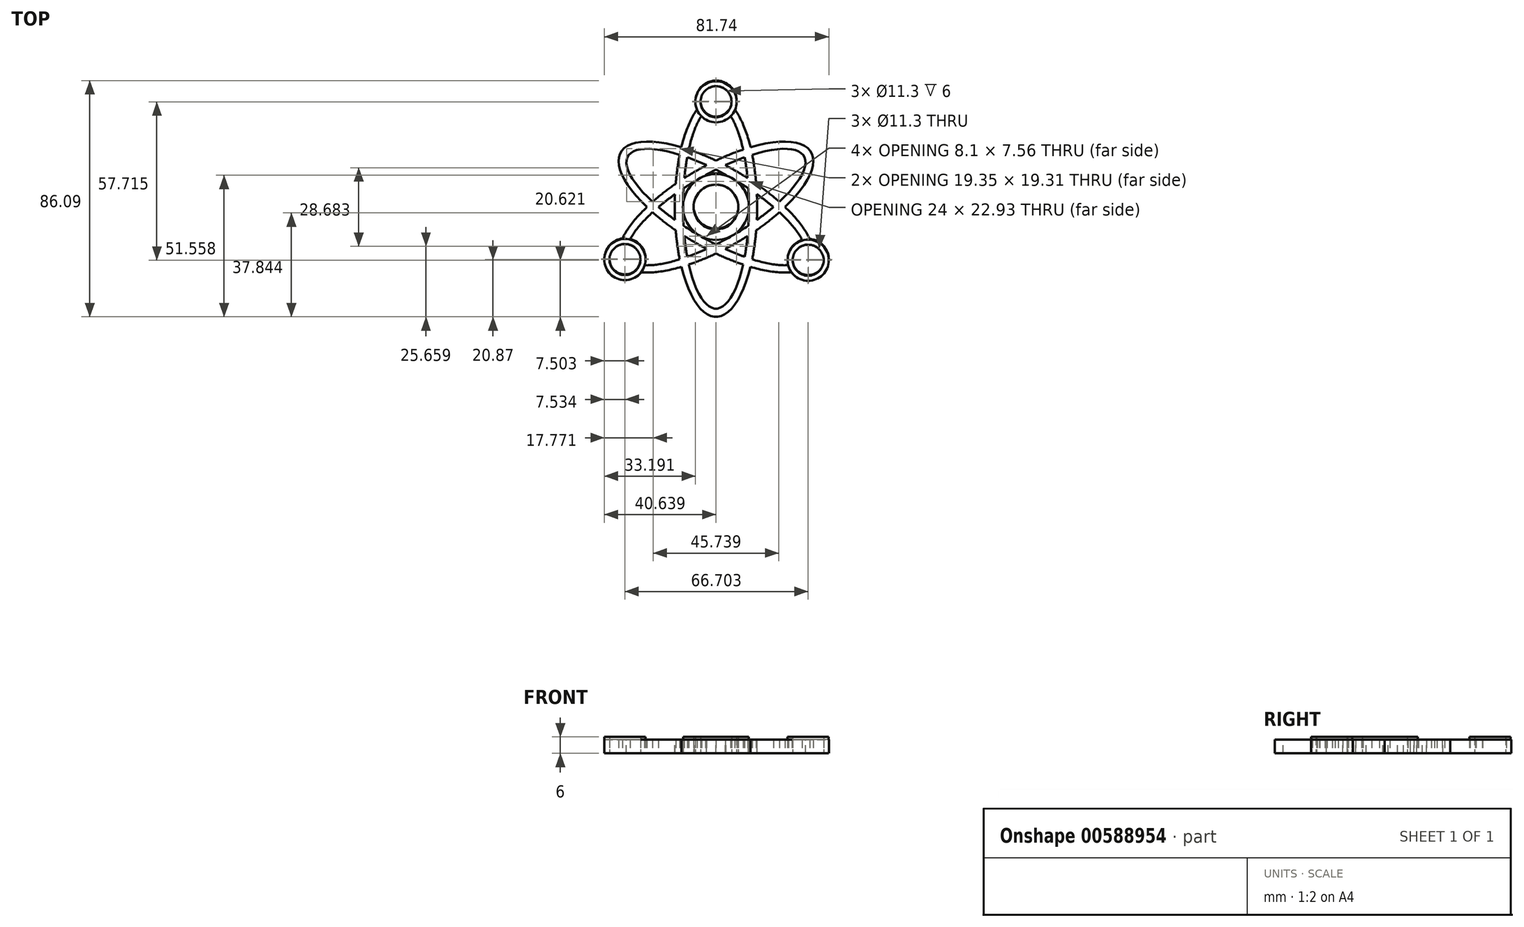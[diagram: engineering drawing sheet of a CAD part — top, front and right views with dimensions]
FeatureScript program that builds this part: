
annotation { "Feature Type Name" : "Feature", "Feature Type Description" : "" }
export const myFeature = defineFeature(function(context is Context, id is Id, definition is map)
    precondition{}
    {
        {
            var Q0;
            Q0=qCreatedBy(makeId("Top.planeOp"),FACE);
            var sketch = newSketch(context, id + "F0", { "sketchPlane" : qUnion([Q0])});
            skEllipticalArc(sketch, "E0", {});
            skEllipticalArc(sketch, "E1", {});
            skEllipticalArc(sketch, "E2", {});
            skEllipticalArc(sketch, "E3", {});
            skEllipticalArc(sketch, "E4", {});
            skEllipticalArc(sketch, "E5", {});
            skEllipticalArc(sketch, "E6.trimOffspring", {});
            skEllipticalArc(sketch, "E7.trimOffspring", {});
            skEllipticalArc(sketch, "E8.trimOffspring", {});
            skEllipticalArc(sketch, "E9.trimOffspring", {});
            skEllipticalArc(sketch, "E10.trimOffspring", {});
            skEllipticalArc(sketch, "E11.trimOffspring", {});
            skEllipticalArc(sketch, "E12.trimOffspring", {});
            skEllipticalArc(sketch, "E13.trimOffspring", {});
            skEllipticalArc(sketch, "E14.trimOffspring", {});
            skEllipticalArc(sketch, "E15.trimOffspring", {});
            skEllipticalArc(sketch, "E16.trimOffspring", {});
            skEllipticalArc(sketch, "E17.trimOffspring", {});
            skEllipticalArc(sketch, "E18.trimOffspring", {});
            skEllipticalArc(sketch, "E19.trimOffspring", {});
            skEllipticalArc(sketch, "E20.trimOffspring", {});
            skEllipticalArc(sketch, "E21.trimOffspring", {});
            skEllipticalArc(sketch, "E22.trimOffspring", {});
            skEllipticalArc(sketch, "E23.trimOffspring", {});
            skEllipticalArc(sketch, "E24.trimOffspring", {});
            skEllipticalArc(sketch, "E25.trimOffspring", {});
            skEllipticalArc(sketch, "E26.trimOffspring", {});
            skEllipticalArc(sketch, "E27.trimOffspring", {});
            skEllipticalArc(sketch, "E28.trimOffspring", {});
            skEllipticalArc(sketch, "E29.trimOffspring", {});
            skEllipticalArc(sketch, "E30.trimOffspring", {});
            skEllipticalArc(sketch, "E31.trimOffspring", {});
            skEllipticalArc(sketch, "E32.trimOffspring", {});
            skEllipticalArc(sketch, "E33.trimOffspring", {});
            skEllipticalArc(sketch, "E34.trimOffspring", {});
            skEllipticalArc(sketch, "E35.trimOffspring", {});
            skEllipticalArc(sketch, "E36.trimOffspring", {});
            skEllipticalArc(sketch, "E37.trimOffspring", {});
            skEllipticalArc(sketch, "E38.trimOffspring", {});
            skEllipticalArc(sketch, "E39.trimOffspring", {});
            skEllipticalArc(sketch, "E40.trimOffspring", {});
            skEllipticalArc(sketch, "E41.trimOffspring", {});
            skEllipticalArc(sketch, "E42.trimOffspring", {});
            skEllipticalArc(sketch, "E43.trimOffspring", {});
            skEllipticalArc(sketch, "E44.trimOffspring", {});
            skEllipticalArc(sketch, "E45.trimOffspring", {});
            skEllipticalArc(sketch, "E46.trimOffspring", {});
            skEllipticalArc(sketch, "E47.trimOffspring", {});
            skCircle(sketch, "E48", {"center": v(0.06, 38.59) * mm, "radius": 7.5 * mm});
            skCircle(sketch, "E49", {"center": v(0.06, 38.59) * mm, "radius": 5.65 * mm});
            skLineSegment(sketch, "E50", {"start": v(37.37, 21.8) * mm, "end": v(-40.19, -22.97) * mm, "construction": true});
            skLineSegment(sketch, "E51", {"start": v(-37.49, 21.91) * mm, "end": v(37.91, -21.62) * mm, "construction": true});
            skLineSegment(sketch, "E52", {"start": v(0.03, 42.33) * mm, "end": v(0.03, -44.74) * mm, "construction": true});
            skCircle(sketch, "E53", {"center": v(33.6, -19.13) * mm, "radius": 7.5 * mm});
            skCircle(sketch, "E54", {"center": v(33.6, -19.13) * mm, "radius": 5.65 * mm});
            skCircle(sketch, "E55", {"center": v(-33.1, -18.88) * mm, "radius": 7.5 * mm});
            skCircle(sketch, "E56", {"center": v(-33.1, -18.88) * mm, "radius": 5.65 * mm});
            skArc(sketch, "E57", {"start": v(3.75, 11.66) * mm, "mid": v(-0.05, 12.25) * mm, "end": v(-3.85, 11.6) * mm});
            skCircle(sketch, "E58", {"center": v(0.03, 0.25) * mm, "radius": 8.15 * mm});
            skEllipticalArc(sketch, "E59.trimOffspring", {});
            skEllipticalArc(sketch, "E60.trimOffspring", {});
            skEllipticalArc(sketch, "E61.trimOffspring", {});
            skEllipticalArc(sketch, "E62.trimOffspring", {});
            skEllipticalArc(sketch, "E63.trimOffspring", {});
            skEllipticalArc(sketch, "E64.trimOffspring", {});
            skEllipticalArc(sketch, "E65.trimOffspring", {});
            skEllipticalArc(sketch, "E66.trimOffspring", {});
            skArc(sketch, "E67.trimOffspring", {"start": v(-7.84, 9.3) * mm, "mid": v(-5.35, -10.48) * mm, "end": v(12, -0.65) * mm});
            skArc(sketch, "E68.trimOffspring", {"start": v(12, 1.2) * mm, "mid": v(10.78, 5.58) * mm, "end": v(8.04, 9.19) * mm});
            skEllipticalArc(sketch, "E69.trimOffspring", {});
            const initialGuessF0  = {"E0": [0, 0, 0, -1, 0.04, 0.015, 4.216313915768055, 4.49917347055926], "E1": [0, 0, 0, -1, 0.037, 0.012, 4.2005723181204395, 4.422913051335495], "E2": [0, 0, -0.8660254037844386, -0.5, 0.04, 0.015, 4.595143205675615, 4.829634755093763], "E3": [0, 0, -0.8660254037844386, -0.5, 0.037, 0.012, 4.527283771982562, 4.6455055557762], "E4": [0, 0, 0.8660254037844386, -0.5, 0.04, 0.015, 2.146833373142214, 4.136351934037372], "E5": [0, 0, 0.8660254037844387, -0.5, 0.037, 0.012, 2.1725088272016655, 4.11067647997792], "E6.trimOffspring": [0, 0, 0.8660254037844386, -0.5, 0.04, 0.015, 1.7840118366203264, 2.066871391411529], "E7.trimOffspring": [0, 0, 0.8660254037844387, -0.5, 0.037, 0.012, 1.8602722558440892, 2.082612989059147], "E8.trimOffspring": [0, 0, 0, -1, 0.037, 0.012, 2.172508827201664, 2.6850580061765315], "E9.trimOffspring": [0, 0, 0, -1, 0.04, 0.015, 2.146833373142215, 2.663481630446535], "E10.trimOffspring": [0, 0, -0.8660254037844386, -0.5, 0.037, 0.012, 4.2005723181204395, 4.422913051335495], "E11.trimOffspring": [0, 0, -0.8660254037844386, -0.5, 0.04, 0.015, 4.2163139157680565, 4.49917347055926], "E12.trimOffspring": [0, 0, -0.8660254037844386, -0.5, 0.04, 0.015, 5.288426026732006, 5.788873073713293], "E13.trimOffspring": [0, 0, 0.8660254037844387, -0.5, 0.037, 0.012, 4.2005723181204395, 4.422913051335495], "E14.trimOffspring": [0, 0, 0.8660254037844386, -0.5, 0.04, 0.015, 4.216313915768058, 4.49917347055926], "E15.trimOffspring": [0, 0, -0.8660254037844386, -0.5, 0.037, 0.012, 5.314101480791458, 5.80419960682295], "E16.trimOffspring": [0, 0, 0.8660254037844387, -0.5, 0.037, 0.012, 4.527283771982562, 4.897494188786816], "E17.trimOffspring": [0, 0, 0, -1, 0.04, 0.015, 4.9256044902101195, 5.208464045001322], "E18.trimOffspring": [0, 0, 0, -1, 0.037, 0.012, 5.001864909433884, 5.22420564264894], "E19.trimOffspring": [0, 0, 0.8660254037844386, -0.5, 0.04, 0.015, 4.595143205675616, 4.829634755093763], "E20.trimOffspring": [0, 0, -0.8660254037844386, -0.5, 0.037, 0.012, 1.058979664530646, 1.281320397745702], "E21.trimOffspring": [0, 0, 0, -1, 0.04, 0.015, 5.288426026732007, 0.9947592804475791], "E22.trimOffspring": [0, 0, 0, -1, 0.037, 0.012, 5.314101480791458, 0.9690838263881281], "E23.trimOffspring": [0, 0, -0.8660254037844386, -0.5, 0.04, 0.015, 1.0747212621782634, 1.3575808169694665], "E24.trimOffspring": [0, 0, -0.8660254037844386, -0.5, 0.037, 0.012, 1.3856911183927698, 1.755901535197023], "E25.trimOffspring": [0, 0, 0.8660254037844386, -0.5, 0.04, 0.015, 4.9256044902101195, 5.208464045001322], "E26.trimOffspring": [0, 0, 0.8660254037844387, -0.5, 0.037, 0.012, 5.001864909433884, 5.22420564264894], "E27.trimOffspring": [0, 0, -0.8660254037844386, -0.5, 0.04, 0.015, 1.453550552085823, 1.68804210150397], "E28.trimOffspring": [0, 0, 0, -1, 0.037, 0.012, 1.0589796645306455, 1.2813203977457022], "E29.trimOffspring": [0, 0, 0.8660254037844387, -0.5, 0.037, 0.012, 5.314101480791457, 5.840267002115699], "E30.trimOffspring": [0, 0, 0, -1, 0.04, 0.015, 1.0747212621782642, 1.3575808169694672], "E31.trimOffspring": [0, 0, 0.8660254037844386, -0.5, 0.04, 0.015, 5.288426026732006, 5.820320072529435], "E32.trimOffspring": [0, 0, 0, -1, 0.037, 0.012, 1.3856911183927698, 1.5532494661964573], "E33.trimOffspring": [0, 0, 0, -1, 0.04, 0.015, 1.4535505520858234, 1.68804210150397], "E34.trimOffspring": [0, 0, -0.8660254037844386, -0.5, 0.037, 0.012, 1.860272255844091, 2.082612989059147], "E35.trimOffspring": [0, 0, -0.8660254037844386, -0.5, 0.04, 0.015, 1.7840118366203266, 2.066871391411528], "E36.trimOffspring": [0, 0, 0, -1, 0.04, 0.015, 1.7840118366203266, 2.0668713914115298], "E37.trimOffspring": [0, 0, 0, -1, 0.037, 0.012, 1.8602722558440905, 2.0826129890591467], "E38.trimOffspring": [0, 0, 0.8660254037844387, -0.5, 0.037, 0.012, 1.3856911183927698, 1.506716611585425], "E39.trimOffspring": [0, 0, 0.8660254037844386, -0.5, 0.04, 0.015, 1.4535505520858232, 1.68804210150397], "E40.trimOffspring": [0, 0, -0.8660254037844386, -0.5, 0.04, 0.015, 2.1468333731422136, 4.136351934037371], "E41.trimOffspring": [0, 0, 0.8660254037844387, -0.5, 0.037, 0.012, 1.0589796645306464, 1.2813203977457022], "E42.trimOffspring": [0, 0, 0.8660254037844386, -0.5, 0.04, 0.015, 1.074721262178265, 1.3575808169694668], "E43.trimOffspring": [0, 0, -0.8660254037844386, -0.5, 0.037, 0.012, 2.172508827201665, 4.11067647997792], "E44.trimOffspring": [0, 0, -0.8660254037844386, -0.5, 0.04, 0.015, 4.9256044902101195, 5.208464045001323], "E45.trimOffspring": [0, 0, 0, -1, 0.037, 0.012, 4.527283771982562, 4.8974941887868155], "E46.trimOffspring": [0, 0, 0, -1, 0.04, 0.015, 4.595143205675616, 4.829634755093763], "E47.trimOffspring": [0, 0, -0.8660254037844386, -0.5, 0.037, 0.012, 5.001864909433884, 5.22420564264894], "E59.trimOffspring": [0, 0, 0, -1, 0.037, 0.012, 3.5938067732776195, 4.110676479977921], "E60.trimOffspring": [0, 0, 0, -1, 0.04, 0.015, 3.614200553282336, 4.136351934037371], "E61.trimOffspring": [0, 0, 0.8660254037844387, -0.5, 0.037, 0.012, 0.4598507042844533, 0.9690838263881281], "E62.trimOffspring": [0, 0, 0.8660254037844386, -0.5, 0.04, 0.015, 0.484379177421726, 0.9947592804475789], "E63.trimOffspring": [0, 0, -0.8660254037844386, -0.5, 0.037, 0.012, 0.46395047352900265, 0.9690838263881275], "E64.trimOffspring": [0, 0, -0.8660254037844386, -0.5, 0.04, 0.015, 0.47484811488574347, 0.9947592804475789], "E65.trimOffspring": [0, 0, -0.8660254037844386, -0.5, 0.037, 0.012, 4.770087493576998, 4.8974941887868155], "E66.trimOffspring": [0, 0, 0.8660254037844387, -0.5, 0.037, 0.012, 1.6407321764099922, 1.7559015351970242], "E69.trimOffspring": [0, 0, 0, -1, 0.037, 0.012, 1.6033846696696494, 1.755901535197024]};
            skSetInitialGuess(sketch, initialGuessF0);
            skSolve(sketch);
        }
        {
            var Q0;
            Q0=qCreatedBy(makeId("Top.planeOp"),FACE);
            var sketch = newSketch(context, id + "F1", { "sketchPlane" : qUnion([Q0])});
            skCircle(sketch, "E70", {"center": v(0.03, 38.34) * mm, "radius": 7.5 * mm});
            skCircle(sketch, "E71", {"center": v(0.03, 38.34) * mm, "radius": 5.65 * mm});
            skLineSegment(sketch, "E72", {"start": v(37.34, 21.56) * mm, "end": v(-40.22, -23.22) * mm, "construction": true});
            skLineSegment(sketch, "E73", {"start": v(-37.52, 21.66) * mm, "end": v(37.88, -21.87) * mm, "construction": true});
            skLineSegment(sketch, "E74", {"start": v(0, 42.08) * mm, "end": v(0, -44.99) * mm, "construction": true});
            skCircle(sketch, "E75", {"center": v(33.57, -19.38) * mm, "radius": 7.5 * mm});
            skCircle(sketch, "E76", {"center": v(33.57, -19.38) * mm, "radius": 5.65 * mm});
            skCircle(sketch, "E77", {"center": v(-33.14, -19.13) * mm, "radius": 7.5 * mm});
            skCircle(sketch, "E78", {"center": v(-33.14, -19.13) * mm, "radius": 5.65 * mm});
            skCircle(sketch, "E79", {"center": v(0, 0) * mm, "radius": 12 * mm});
            skCircle(sketch, "E80", {"center": v(0, 0) * mm, "radius": 8.15 * mm});
            skSolve(sketch);
        }
        {
            var Q0;
            Q0=makeQuery(id+"F1.imprint","IMPRINT",FACE,{"disambiguationData":[TD([[makeQuery(id+"F1.imprint","IMPRINT",EDGE,{"derivedFrom":sQuery(id+"F1.wireOp",EDGE,"E79")}),1.0]])]});
            var Q1;
            Q1=makeQuery(id+"F1.imprint","IMPRINT",FACE,{"disambiguationData":[TD([[makeQuery(id+"F1.imprint","IMPRINT",EDGE,{"derivedFrom":sQuery(id+"F1.wireOp",EDGE,"E77")}),1.0]])]});
            var Q2;
            Q2=makeQuery(id+"F1.imprint","IMPRINT",FACE,{"disambiguationData":[TD([[makeQuery(id+"F1.imprint","IMPRINT",EDGE,{"derivedFrom":sQuery(id+"F1.wireOp",EDGE,"E75")}),1.0]])]});
            var Q3;
            Q3=makeQuery(id+"F1.imprint","IMPRINT",FACE,{"disambiguationData":[TD([[makeQuery(id+"F1.imprint","IMPRINT",EDGE,{"derivedFrom":sQuery(id+"F1.wireOp",EDGE,"E70")}),1.0]])]});
            extrude(context, id + "F2", {"entities" : qUnion([Q0, Q1, Q2, Q3]), "depth" : 6 * mm, "offsetDistance" : 25 * mm});
        }
        {
            var Q0;
            Q0 = qSketchRegion(id + "F0", true);
            extrude(context, id + "F3", {"entities" : qUnion([Q0]), "depth" : 5 * mm, "offsetDistance" : 25 * mm});
        }
    });
